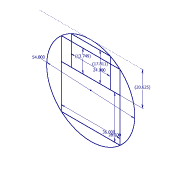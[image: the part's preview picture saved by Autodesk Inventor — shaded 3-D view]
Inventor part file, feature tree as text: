
AUTODESK INVENTOR PART (.ipt)
format: ipt  version: 2012 (Build 160160000, 160)  size: 67,584 bytes
history: native  units: in
note: dims shown in document units (in); Inventor stores cm internally (conversion verified against a paired STEP export)
features: sketch x1
ambient origin geometry x8: Origin, YZ Plane, XZ Plane, XY Plane, X Axis, Y Axis, Z Axis, Center Point
feature tree (1):
  sketch  "Sketch1"  dims[d0=54.0in d1=36.0in d2=26.5in d3=20.6246in d5=13.7492in d6=24.0in d7=17.8114in]
